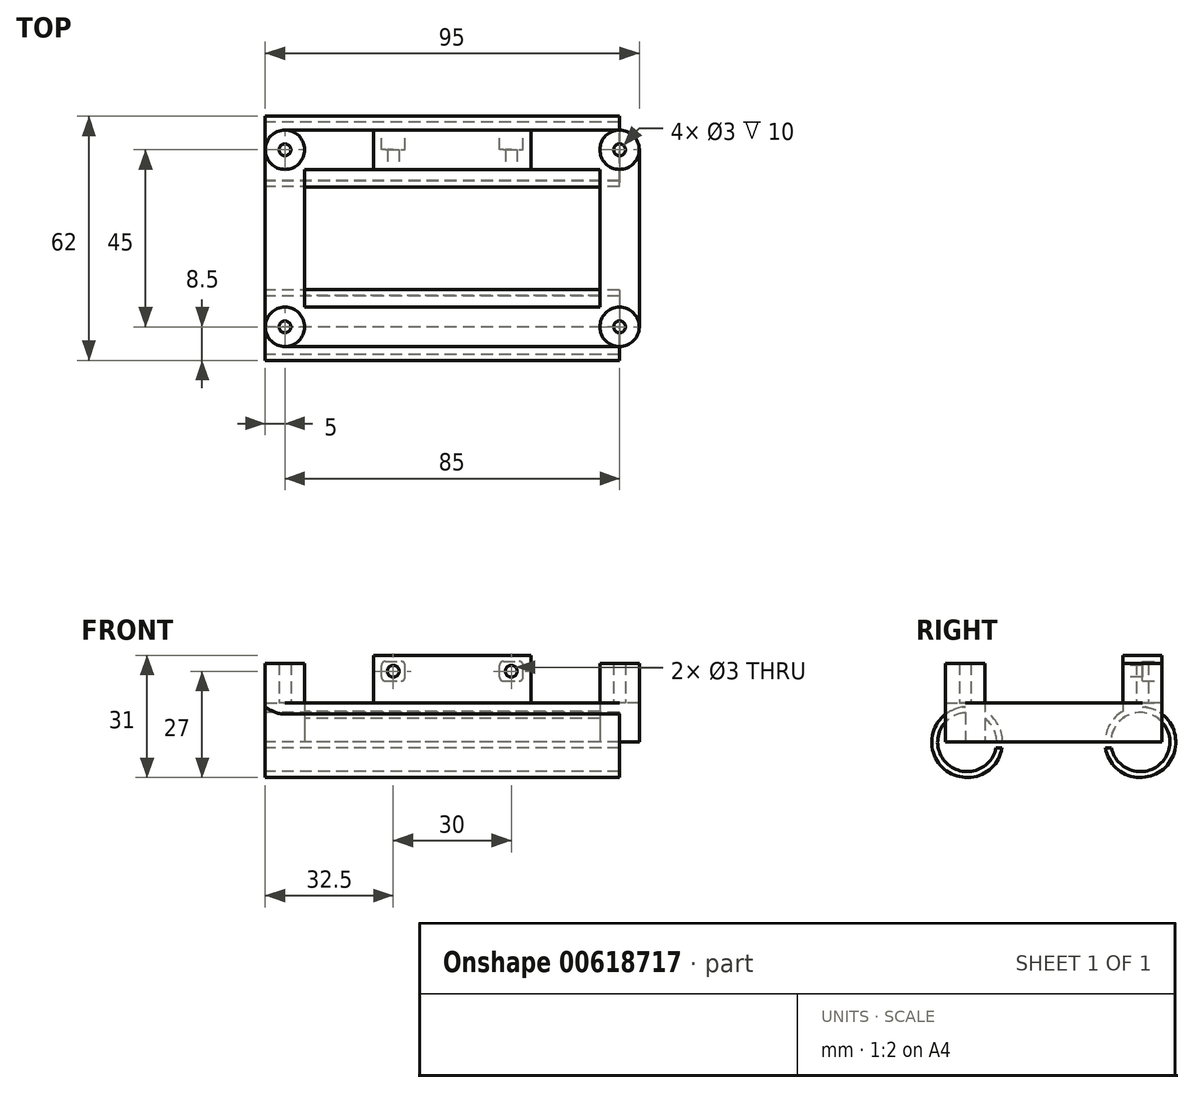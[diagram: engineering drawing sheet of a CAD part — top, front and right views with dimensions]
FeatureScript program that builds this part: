
annotation { "Feature Type Name" : "Feature", "Feature Type Description" : "" }
export const myFeature = defineFeature(function(context is Context, id is Id, definition is map)
    precondition{}
    {
        {
            var Q0;
            Q0=qCreatedBy(makeId("Top.planeOp"),FACE);
            var sketch = newSketch(context, id + "F0", { "sketchPlane" : qUnion([Q0])});
            skLineSegment(sketch, "E0.bottom", {"start": v(37.5, -17.5) * mm, "end": v(-37.5, -17.5) * mm});
            skLineSegment(sketch, "E0.top", {"start": v(37.5, 17.5) * mm, "end": v(-37.5, 17.5) * mm});
            skLineSegment(sketch, "E0.left", {"start": v(37.5, -17.5) * mm, "end": v(37.5, 17.5) * mm});
            skLineSegment(sketch, "E0.right", {"start": v(-37.5, -17.5) * mm, "end": v(-37.5, 17.5) * mm});
            skPoint(sketch, "E0.middle", {"position": v(0, 0) * mm});
            skLineSegment(sketch, "E1.bottom", {"start": v(47.5, -27.5) * mm, "end": v(-47.5, -27.5) * mm});
            skLineSegment(sketch, "E1.top", {"start": v(47.5, 27.5) * mm, "end": v(-47.5, 27.5) * mm});
            skLineSegment(sketch, "E1.left", {"start": v(47.5, -27.5) * mm, "end": v(47.5, 27.5) * mm});
            skLineSegment(sketch, "E1.right", {"start": v(-47.5, -27.5) * mm, "end": v(-47.5, 27.5) * mm});
            skLineSegment(sketch, "E2", {"start": v(0, 17.5) * mm, "end": v(0, 27.5) * mm, "construction": true});
            skSolve(sketch);
        }
        {
            var Q0;
            Q0=makeQuery(id+"F0.imprint","IMPRINT",FACE,{"disambiguationData":[TD([[makeQuery(id+"F0.imprint","IMPRINT",EDGE,{"derivedFrom":sQuery(id+"F0.wireOp",EDGE,"E0.bottom")}),1.0]])]});
            extrude(context, id + "F1", {"entities" : qUnion([Q0]), "depth" : 10 * mm, "offsetDistance" : 25 * mm});
        }
        {
            var Q0;
            Q0=makeQuery(id+"F1.opExtrude","SWEPT_EDGE",EDGE,{"disambiguationData":[OSD([sQuery(id+"F0.wireOp",EDGE,"E1.bottom"),sQuery(id+"F0.wireOp",EDGE,"E1.right")])]});
            var Q1;
            Q1=makeQuery(id+"F1.opExtrude","SWEPT_EDGE",EDGE,{"disambiguationData":[OSD([sQuery(id+"F0.wireOp",EDGE,"E1.bottom"),sQuery(id+"F0.wireOp",EDGE,"E1.left")])]});
            var Q2;
            Q2=makeQuery(id+"F1.opExtrude","SWEPT_EDGE",EDGE,{"disambiguationData":[OSD([sQuery(id+"F0.wireOp",EDGE,"E1.top"),sQuery(id+"F0.wireOp",EDGE,"E1.left")])]});
            var Q3;
            Q3=makeQuery(id+"F1.opExtrude","SWEPT_EDGE",EDGE,{"disambiguationData":[OSD([sQuery(id+"F0.wireOp",EDGE,"E1.top"),sQuery(id+"F0.wireOp",EDGE,"E1.right")])]});
            fillet(context, id + "F2", {"entities" : qUnion([Q0, Q1, Q2, Q3]), "radius" : 5 * mm, "tangentPropagation" : true, "allowEdgeOverflow" : false});
        }
        {
            var Q0;
            Q0=makeQuery(id+"F1.opExtrude","CAP_FACE",FACE,{"disambiguationData":[OSD([sQuery(id+"F0.wireOp",EDGE,"E0.bottom"),sQuery(id+"F0.wireOp",EDGE,"E0.top"),sQuery(id+"F0.wireOp",EDGE,"E0.left"),sQuery(id+"F0.wireOp",EDGE,"E0.right"),sQuery(id+"F0.wireOp",EDGE,"E1.bottom"),sQuery(id+"F0.wireOp",EDGE,"E1.top"),sQuery(id+"F0.wireOp",EDGE,"E1.left"),sQuery(id+"F0.wireOp",EDGE,"E1.right")])],"isStart":false});
            var sketch = newSketch(context, id + "F3", { "sketchPlane" : qUnion([Q0])});
            skLineSegment(sketch, "E3.bottom", {"start": v(20, 17.5) * mm, "end": v(-20, 17.5) * mm});
            skLineSegment(sketch, "E3.top", {"start": v(20, 27.5) * mm, "end": v(-20, 27.5) * mm});
            skLineSegment(sketch, "E3.left", {"start": v(20, 17.5) * mm, "end": v(20, 27.5) * mm});
            skLineSegment(sketch, "E3.right", {"start": v(-20, 17.5) * mm, "end": v(-20, 27.5) * mm});
            skPoint(sketch, "E3.middle", {"position": v(0, 22.5) * mm});
            skSolve(sketch);
        }
        {
            var Q0;
            Q0=makeQuery(id+"F3.imprint","IMPRINT",FACE,{"disambiguationData":[TD([[makeQuery(id+"F3.imprint","IMPRINT",EDGE,{"derivedFrom":sQuery(id+"F3.wireOp",EDGE,"E3.bottom")}),-1.0]])]});
            extrude(context, id + "F4", {"entities" : qUnion([Q0]), "operationType" : NewBodyOperationType.ADD, "depth" : 12 * mm, "offsetDistance" : 25 * mm});
        }
        {
            var Q0;
            Q0=makeQuery(id+"F4.boolean.opBoolean","MERGE",FACE,{"derivedFrom":[makeQuery(id+"F1.opExtrude","SWEPT_FACE",FACE,{"disambiguationData":[OSD([sQuery(id+"F0.wireOp",EDGE,"E0.top")])]}),makeQuery(id+"F4.opExtrude","SWEPT_FACE",FACE,{"disambiguationData":[OSD([sQuery(id+"F3.wireOp",EDGE,"E3.bottom")])]})]});
            var sketch = newSketch(context, id + "F5", { "sketchPlane" : qUnion([Q0])});
            skCircle(sketch, "E4", {"center": v(-15, 18) * mm, "radius": 1.5 * mm});
            skCircle(sketch, "E5", {"center": v(15, 18) * mm, "radius": 1.5 * mm});
            skLineSegment(sketch, "E6", {"start": v(-15, 18) * mm, "end": v(15, 18) * mm, "construction": true});
            skLineSegment(sketch, "E7", {"start": v(0, 18) * mm, "end": v(0, 10) * mm, "construction": true});
            skSolve(sketch);
        }
        {
            var Q0;
            Q0=makeQuery(id+"F5.imprint","IMPRINT",FACE,{"disambiguationData":[TD([[makeQuery(id+"F5.imprint","IMPRINT",EDGE,{"derivedFrom":sQuery(id+"F5.wireOp",EDGE,"E4")}),1.0]])]});
            var Q1;
            Q1=makeQuery(id+"F5.imprint","IMPRINT",FACE,{"disambiguationData":[TD([[makeQuery(id+"F5.imprint","IMPRINT",EDGE,{"derivedFrom":sQuery(id+"F5.wireOp",EDGE,"E5")}),1.0]])]});
            var Q2;
            Q2=sQuery(id+"F5.wireOp",EDGE,"E7");
            var Q3;
            Q3=sQuery(id+"F5.wireOp",EDGE,"E6");
            var Q4;
            Q4=sQuery(id+"F5.wireOp",EDGE,"E4");
            var Q5;
            Q5=sQuery(id+"F5.wireOp",EDGE,"E5");
            extrude(context, id + "F6", {"entities" : qUnion([Q0, Q1]), "operationType" : NewBodyOperationType.REMOVE, "surfaceEntities" : qUnion([Q2, Q3, Q4, Q5]), "oppositeDirection" : true, "depth" : 25 * mm, "offsetDistance" : 25 * mm});
        }
        {
            var Q0;
            Q0=makeQuery(id+"F4.boolean.opBoolean","MERGE",FACE,{"derivedFrom":[makeQuery(id+"F1.opExtrude","SWEPT_FACE",FACE,{"disambiguationData":[OSD([sQuery(id+"F0.wireOp",EDGE,"E1.top")])]}),makeQuery(id+"F4.opExtrude","SWEPT_FACE",FACE,{"disambiguationData":[OSD([sQuery(id+"F3.wireOp",EDGE,"E3.top")])]})]});
            var sketch = newSketch(context, id + "F7", { "sketchPlane" : qUnion([Q0])});
            skLineSegment(sketch, "E8.bottom", {"start": v(-12, 15.5) * mm, "end": v(-18, 15.5) * mm});
            skLineSegment(sketch, "E8.top", {"start": v(-12, 20.5) * mm, "end": v(-18, 20.5) * mm});
            skLineSegment(sketch, "E8.left", {"start": v(-12, 15.5) * mm, "end": v(-12, 20.5) * mm});
            skLineSegment(sketch, "E8.right", {"start": v(-18, 15.5) * mm, "end": v(-18, 20.5) * mm});
            skPoint(sketch, "E8.middle", {"position": v(-15, 18) * mm});
            skLineSegment(sketch, "E9.bottom", {"start": v(18, 15.5) * mm, "end": v(12, 15.5) * mm});
            skLineSegment(sketch, "E9.top", {"start": v(18, 20.5) * mm, "end": v(12, 20.5) * mm});
            skLineSegment(sketch, "E9.left", {"start": v(18, 15.5) * mm, "end": v(18, 20.5) * mm});
            skLineSegment(sketch, "E9.right", {"start": v(12, 15.5) * mm, "end": v(12, 20.5) * mm});
            skPoint(sketch, "E9.middle", {"position": v(15, 18) * mm});
            skSolve(sketch);
        }
        {
            var Q0;
            Q0=makeQuery(id+"F7.imprint","IMPRINT",FACE,{"disambiguationData":[TD([[makeQuery(id+"F7.imprint","IMPRINT",EDGE,{"derivedFrom":makeQuery(id+"F6.boolean.opBoolean","INTERSECT",EDGE,{"derivedFrom":[makeQuery(id+"F4.boolean.opBoolean","MERGE",FACE,{"derivedFrom":[makeQuery(id+"F1.opExtrude","SWEPT_FACE",FACE,{"disambiguationData":[OSD([sQuery(id+"F0.wireOp",EDGE,"E1.top")])]}),makeQuery(id+"F4.opExtrude","SWEPT_FACE",FACE,{"disambiguationData":[OSD([sQuery(id+"F3.wireOp",EDGE,"E3.top")])]})]}),makeQuery(id+"F6.opExtrude","SWEPT_FACE",FACE,{"disambiguationData":[OSD([sQuery(id+"F5.wireOp",EDGE,"E4")])]})]})}),-1.0]])]});
            var Q1;
            Q1=makeQuery(id+"F7.imprint","IMPRINT",FACE,{"disambiguationData":[TD([[makeQuery(id+"F7.imprint","IMPRINT",EDGE,{"derivedFrom":makeQuery(id+"F6.boolean.opBoolean","INTERSECT",EDGE,{"derivedFrom":[makeQuery(id+"F4.boolean.opBoolean","MERGE",FACE,{"derivedFrom":[makeQuery(id+"F1.opExtrude","SWEPT_FACE",FACE,{"disambiguationData":[OSD([sQuery(id+"F0.wireOp",EDGE,"E1.top")])]}),makeQuery(id+"F4.opExtrude","SWEPT_FACE",FACE,{"disambiguationData":[OSD([sQuery(id+"F3.wireOp",EDGE,"E3.top")])]})]}),makeQuery(id+"F6.opExtrude","SWEPT_FACE",FACE,{"disambiguationData":[OSD([sQuery(id+"F5.wireOp",EDGE,"E5")])]})]})}),-1.0]])]});
            var Q2;
            Q2=makeQuery(id+"F7.imprint","IMPRINT",FACE,{"disambiguationData":[TD([[makeQuery(id+"F7.imprint","IMPRINT",EDGE,{"derivedFrom":sQuery(id+"F7.wireOp",EDGE,"E9.bottom")}),-1.0]])]});
            var Q3;
            Q3=makeQuery(id+"F7.imprint","IMPRINT",FACE,{"disambiguationData":[TD([[makeQuery(id+"F7.imprint","IMPRINT",EDGE,{"derivedFrom":sQuery(id+"F7.wireOp",EDGE,"E8.bottom")}),-1.0]])]});
            extrude(context, id + "F8", {"entities" : qUnion([Q0, Q1, Q2, Q3]), "operationType" : NewBodyOperationType.REMOVE, "oppositeDirection" : true, "depth" : 5 * mm, "offsetDistance" : 25 * mm});
        }
        {
            var Q0;
            Q0=makeQuery(id+"F8.boolean.opBoolean","COPY",EDGE,{"derivedFrom":makeQuery(id+"F8.opExtrude","SWEPT_EDGE",EDGE,{"disambiguationData":[OSD([sQuery(id+"F7.wireOp",EDGE,"E8.top"),sQuery(id+"F7.wireOp",EDGE,"E8.right")])]})});
            var Q1;
            Q1=makeQuery(id+"F8.boolean.opBoolean","COPY",EDGE,{"derivedFrom":makeQuery(id+"F8.opExtrude","SWEPT_EDGE",EDGE,{"disambiguationData":[OSD([sQuery(id+"F7.wireOp",EDGE,"E8.top"),sQuery(id+"F7.wireOp",EDGE,"E8.left")])]})});
            var Q2;
            Q2=makeQuery(id+"F8.boolean.opBoolean","COPY",EDGE,{"derivedFrom":makeQuery(id+"F8.opExtrude","SWEPT_EDGE",EDGE,{"disambiguationData":[OSD([sQuery(id+"F7.wireOp",EDGE,"E8.bottom"),sQuery(id+"F7.wireOp",EDGE,"E8.right")])]})});
            var Q3;
            Q3=makeQuery(id+"F8.boolean.opBoolean","COPY",EDGE,{"derivedFrom":makeQuery(id+"F8.opExtrude","SWEPT_EDGE",EDGE,{"disambiguationData":[OSD([sQuery(id+"F7.wireOp",EDGE,"E8.bottom"),sQuery(id+"F7.wireOp",EDGE,"E8.left")])]})});
            var Q4;
            Q4=makeQuery(id+"F8.boolean.opBoolean","COPY",EDGE,{"derivedFrom":makeQuery(id+"F8.opExtrude","SWEPT_EDGE",EDGE,{"disambiguationData":[OSD([sQuery(id+"F7.wireOp",EDGE,"E9.top"),sQuery(id+"F7.wireOp",EDGE,"E9.left")])]})});
            var Q5;
            Q5=makeQuery(id+"F8.boolean.opBoolean","COPY",EDGE,{"derivedFrom":makeQuery(id+"F8.opExtrude","SWEPT_EDGE",EDGE,{"disambiguationData":[OSD([sQuery(id+"F7.wireOp",EDGE,"E9.top"),sQuery(id+"F7.wireOp",EDGE,"E9.right")])]})});
            var Q6;
            Q6=makeQuery(id+"F8.boolean.opBoolean","COPY",EDGE,{"derivedFrom":makeQuery(id+"F8.opExtrude","SWEPT_EDGE",EDGE,{"disambiguationData":[OSD([sQuery(id+"F7.wireOp",EDGE,"E9.bottom"),sQuery(id+"F7.wireOp",EDGE,"E9.right")])]})});
            var Q7;
            Q7=makeQuery(id+"F8.boolean.opBoolean","COPY",EDGE,{"derivedFrom":makeQuery(id+"F8.opExtrude","SWEPT_EDGE",EDGE,{"disambiguationData":[OSD([sQuery(id+"F7.wireOp",EDGE,"E9.bottom"),sQuery(id+"F7.wireOp",EDGE,"E9.left")])]})});
            fillet(context, id + "F9", {"entities" : qUnion([Q0, Q1, Q2, Q3, Q4, Q5, Q6, Q7]), "radius" : 1 * mm, "tangentPropagation" : true, "allowEdgeOverflow" : false});
        }
        {
            var Q0;
            Q0=makeQuery(id+"F1.opExtrude","SWEPT_FACE",FACE,{"disambiguationData":[OSD([sQuery(id+"F0.wireOp",EDGE,"E1.right")])]});
            var sketch = newSketch(context, id + "F10", { "sketchPlane" : qUnion([Q0])});
            skLineSegment(sketch, "E10", {"start": v(0, 0) * mm, "end": v(22, 0) * mm});
            skLineSegment(sketch, "E11", {"start": v(0, 0) * mm, "end": v(-22, 0) * mm});
            skCircle(sketch, "E12", {"center": v(-22, 0) * mm, "radius": 7.5 * mm});
            skCircle(sketch, "E13", {"center": v(22, 0) * mm, "radius": 7.5 * mm});
            skCircle(sketch, "E14", {"center": v(-22, 0) * mm, "radius": 9 * mm});
            skCircle(sketch, "E15", {"center": v(22, 0) * mm, "radius": 9 * mm});
            skSolve(sketch);
        }
        {
            var Q0;
            Q0 = qSketchRegion(id + "F10", true);
            extrude(context, id + "F11", {"entities" : qUnion([Q0]), "operationType" : NewBodyOperationType.ADD, "oppositeDirection" : true, "depth" : 90 * mm, "offsetDistance" : 25 * mm});
        }
        {
            var Q0;
            Q0=makeQuery(id+"F11.boolean.opBoolean","MERGE",FACE,{"derivedFrom":[makeQuery(id+"F1.opExtrude","SWEPT_FACE",FACE,{"disambiguationData":[OSD([sQuery(id+"F0.wireOp",EDGE,"E1.right")])]}),makeQuery(id+"F11.opExtrude","CAP_FACE",FACE,{"disambiguationData":[OSD([sQuery(id+"F10.wireOp",EDGE,"E12"),sQuery(id+"F10.wireOp",EDGE,"E14")])],"isStart":true}),makeQuery(id+"F11.opExtrude","CAP_FACE",FACE,{"disambiguationData":[OSD([sQuery(id+"F10.wireOp",EDGE,"E13"),sQuery(id+"F10.wireOp",EDGE,"E15")])],"isStart":true})]});
            var sketch = newSketch(context, id + "F12", { "sketchPlane" : qUnion([Q0])});
            skCircle(sketch, "E16", {"center": v(-22, 0) * mm, "radius": 7.5 * mm});
            skCircle(sketch, "E17", {"center": v(22, 0) * mm, "radius": 7.5 * mm});
            skLineSegment(sketch, "E18.bottom", {"start": v(-14.5, 0) * mm, "end": v(14.5, 0) * mm});
            skLineSegment(sketch, "E18.top", {"start": v(-14.5, -1.5) * mm, "end": v(14.5, -1.5) * mm});
            skLineSegment(sketch, "E18.left", {"start": v(-14.5, 0) * mm, "end": v(-14.5, -1.5) * mm});
            skLineSegment(sketch, "E18.right", {"start": v(14.5, 0) * mm, "end": v(14.5, -1.5) * mm});
            skLineSegment(sketch, "E19", {"start": v(-14.5, -1.5) * mm, "end": v(-15.33, -1.5) * mm});
            skLineSegment(sketch, "E20", {"start": v(-15.33, -1.5) * mm, "end": v(-15.33, 0) * mm});
            skLineSegment(sketch, "E21", {"start": v(-15.33, 0) * mm, "end": v(-14.5, 0) * mm});
            skLineSegment(sketch, "E22.bottom", {"start": v(14.5, 0) * mm, "end": v(15.74, 0) * mm});
            skLineSegment(sketch, "E22.top", {"start": v(14.5, 0) * mm, "end": v(15.74, 0) * mm});
            skLineSegment(sketch, "E22.left", {"start": v(14.5, 0) * mm, "end": v(14.5, 0) * mm});
            skLineSegment(sketch, "E22.right", {"start": v(15.74, 0) * mm, "end": v(15.74, 0) * mm});
            skLineSegment(sketch, "E23", {"start": v(14.5, -1.5) * mm, "end": v(15.74, -1.5) * mm});
            skLineSegment(sketch, "E24", {"start": v(15.74, -1.5) * mm, "end": v(15.74, 0) * mm});
            skSolve(sketch);
        }
        {
            var Q0;
            {var subQ11=sQuery(id+"F12.wireOp",EDGE,"E21");Q0=makeQuery(id+"F12.imprint","IMPRINT",FACE,{"disambiguationData":[TD([[makeQuery(id+"F12.imprint","IMPRINT",EDGE,{"derivedFrom":subQ11}),-1.0]])]});}
            var Q1;
            {var subQ0=sQuery(id+"F12.wireOp",EDGE,"E18.left");Q1=makeQuery(id+"F12.imprint","IMPRINT",FACE,{"disambiguationData":[TD([[makeQuery(id+"F12.imprint","IMPRINT",EDGE,{"derivedFrom":subQ0}),-1.0]])]});}
            var Q2;
            {var subQ11=sQuery(id+"F12.wireOp",EDGE,"E22.top");Q2=makeQuery(id+"F12.imprint","IMPRINT",FACE,{"disambiguationData":[TD([[makeQuery(id+"F12.imprint","IMPRINT",EDGE,{"derivedFrom":subQ11}),-1.0]])]});}
            var Q3;
            {var subQ0=sQuery(id+"F12.wireOp",EDGE,"E18.right");Q3=makeQuery(id+"F12.imprint","IMPRINT",FACE,{"disambiguationData":[TD([[makeQuery(id+"F12.imprint","IMPRINT",EDGE,{"derivedFrom":subQ0}),1.0]])]});}
            var Q4;
            {var subQ0=sQuery(id+"F12.wireOp",EDGE,"E22.top");Q4=makeQuery(id+"F12.imprint","IMPRINT",FACE,{"disambiguationData":[TD([[makeQuery(id+"F12.imprint","IMPRINT",EDGE,{"derivedFrom":subQ0}),1.0]])]});}
            var Q5;
            {var subQ0=sQuery(id+"F12.wireOp",EDGE,"E18.right");Q5=makeQuery(id+"F12.imprint","IMPRINT",FACE,{"disambiguationData":[TD([[makeQuery(id+"F12.imprint","IMPRINT",EDGE,{"derivedFrom":subQ0}),-1.0]])]});}
            var Q6;
            {var subQ0=sQuery(id+"F12.wireOp",EDGE,"E18.left");Q6=makeQuery(id+"F12.imprint","IMPRINT",FACE,{"disambiguationData":[TD([[makeQuery(id+"F12.imprint","IMPRINT",EDGE,{"derivedFrom":subQ0}),1.0]])]});}
            var Q7;
            {var subQ10=sQuery(id+"F12.wireOp",EDGE,"E20");Q7=makeQuery(id+"F12.imprint","IMPRINT",FACE,{"disambiguationData":[TD([[makeQuery(id+"F12.imprint","IMPRINT",EDGE,{"derivedFrom":subQ10}),1.0]])]});}
            var Q8;
            {var subQ10=sQuery(id+"F12.wireOp",EDGE,"E24");Q8=makeQuery(id+"F12.imprint","IMPRINT",FACE,{"disambiguationData":[TD([[makeQuery(id+"F12.imprint","IMPRINT",EDGE,{"derivedFrom":subQ10}),-1.0]])]});}
            extrude(context, id + "F13", {"entities" : qUnion([Q0, Q1, Q2, Q3, Q4, Q5, Q6, Q7, Q8]), "operationType" : NewBodyOperationType.REMOVE, "oppositeDirection" : true, "depth" : 90 * mm, "offsetDistance" : 25 * mm});
        }
        {
            var Q0;
            Q0=makeQuery(id+"F1.opExtrude","CAP_FACE",FACE,{"disambiguationData":[OSD([sQuery(id+"F0.wireOp",EDGE,"E0.bottom"),sQuery(id+"F0.wireOp",EDGE,"E0.top"),sQuery(id+"F0.wireOp",EDGE,"E0.left"),sQuery(id+"F0.wireOp",EDGE,"E0.right"),sQuery(id+"F0.wireOp",EDGE,"E1.bottom"),sQuery(id+"F0.wireOp",EDGE,"E1.top"),sQuery(id+"F0.wireOp",EDGE,"E1.left"),sQuery(id+"F0.wireOp",EDGE,"E1.right")])],"isStart":false});
            var sketch = newSketch(context, id + "F14", { "sketchPlane" : qUnion([Q0])});
            skLineSegment(sketch, "E25.bottom", {"start": v(42.5, -22.5) * mm, "end": v(-42.5, -22.5) * mm, "construction": true});
            skLineSegment(sketch, "E25.top", {"start": v(42.5, 22.5) * mm, "end": v(-42.5, 22.5) * mm, "construction": true});
            skLineSegment(sketch, "E25.left", {"start": v(42.5, -22.5) * mm, "end": v(42.5, 22.5) * mm, "construction": true});
            skLineSegment(sketch, "E25.right", {"start": v(-42.5, -22.5) * mm, "end": v(-42.5, 22.5) * mm, "construction": true});
            skPoint(sketch, "E25.middle", {"position": v(0, 0) * mm});
            skCircle(sketch, "E26", {"center": v(-42.5, -22.5) * mm, "radius": 5 * mm});
            skCircle(sketch, "E27", {"center": v(42.5, -22.5) * mm, "radius": 5 * mm});
            skCircle(sketch, "E28", {"center": v(42.5, 22.5) * mm, "radius": 5 * mm});
            skCircle(sketch, "E29", {"center": v(-42.5, 22.5) * mm, "radius": 5 * mm});
            skCircle(sketch, "E30", {"center": v(-42.5, -22.5) * mm, "radius": 1.5 * mm});
            skCircle(sketch, "E31", {"center": v(42.5, -22.5) * mm, "radius": 1.5 * mm});
            skCircle(sketch, "E32", {"center": v(42.5, 22.5) * mm, "radius": 1.5 * mm});
            skCircle(sketch, "E33", {"center": v(-42.5, 22.5) * mm, "radius": 1.5 * mm});
            skSolve(sketch);
        }
        {
            var Q0;
            Q0=makeQuery(id+"F14.imprint","IMPRINT",FACE,{"disambiguationData":[TD([[makeQuery(id+"F14.imprint","IMPRINT",EDGE,{"derivedFrom":sQuery(id+"F14.wireOp",EDGE,"E33")}),-1.0]])]});
            var Q1;
            Q1=makeQuery(id+"F14.imprint","IMPRINT",FACE,{"disambiguationData":[TD([[makeQuery(id+"F14.imprint","IMPRINT",EDGE,{"derivedFrom":sQuery(id+"F14.wireOp",EDGE,"E30")}),-1.0]])]});
            var Q2;
            Q2=makeQuery(id+"F14.imprint","IMPRINT",FACE,{"disambiguationData":[TD([[makeQuery(id+"F14.imprint","IMPRINT",EDGE,{"derivedFrom":sQuery(id+"F14.wireOp",EDGE,"E31")}),-1.0]])]});
            var Q3;
            Q3=makeQuery(id+"F14.imprint","IMPRINT",FACE,{"disambiguationData":[TD([[makeQuery(id+"F14.imprint","IMPRINT",EDGE,{"derivedFrom":sQuery(id+"F14.wireOp",EDGE,"E32")}),-1.0]])]});
            extrude(context, id + "F15", {"entities" : qUnion([Q0, Q1, Q2, Q3]), "operationType" : NewBodyOperationType.ADD, "depth" : 10 * mm, "offsetDistance" : 25 * mm});
        }
    });
